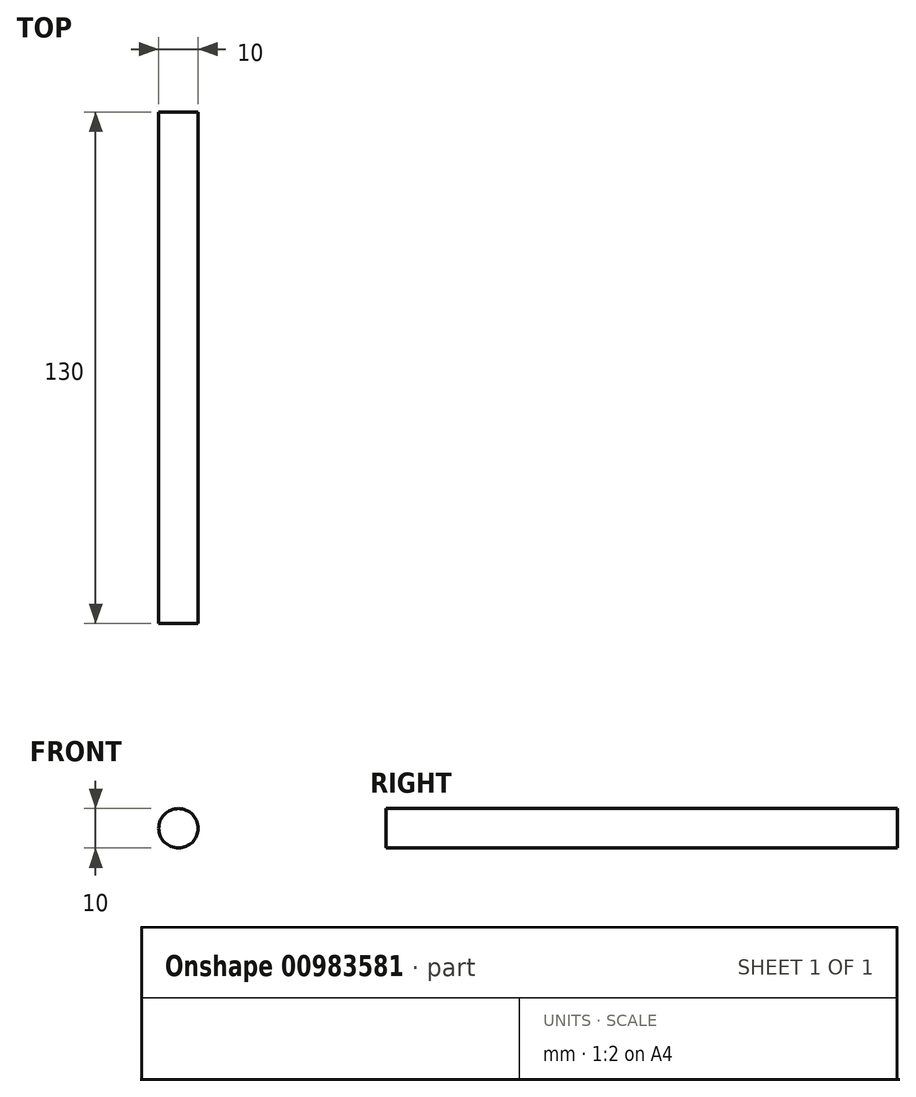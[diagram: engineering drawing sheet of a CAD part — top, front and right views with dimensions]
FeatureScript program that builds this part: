
annotation { "Feature Type Name" : "Feature", "Feature Type Description" : "" }
export const myFeature = defineFeature(function(context is Context, id is Id, definition is map)
    precondition{}
    {
        {
            var Q0;
            Q0=qCreatedBy(makeId("Front.planeOp"),FACE);
            var sketch = newSketch(context, id + "F0", { "sketchPlane" : qUnion([Q0])});
            skCircle(sketch, "E0", {"center": v(0, 0) * mm, "radius": 5 * mm});
            skSolve(sketch);
        }
        {
            var Q0;
            Q0 = qSketchRegion(id + "F0", true);
            extrude(context, id + "F1", {"entities" : qUnion([Q0]), "depth" : 130 * mm, "offsetDistance" : 25 * mm});
        }
    });
